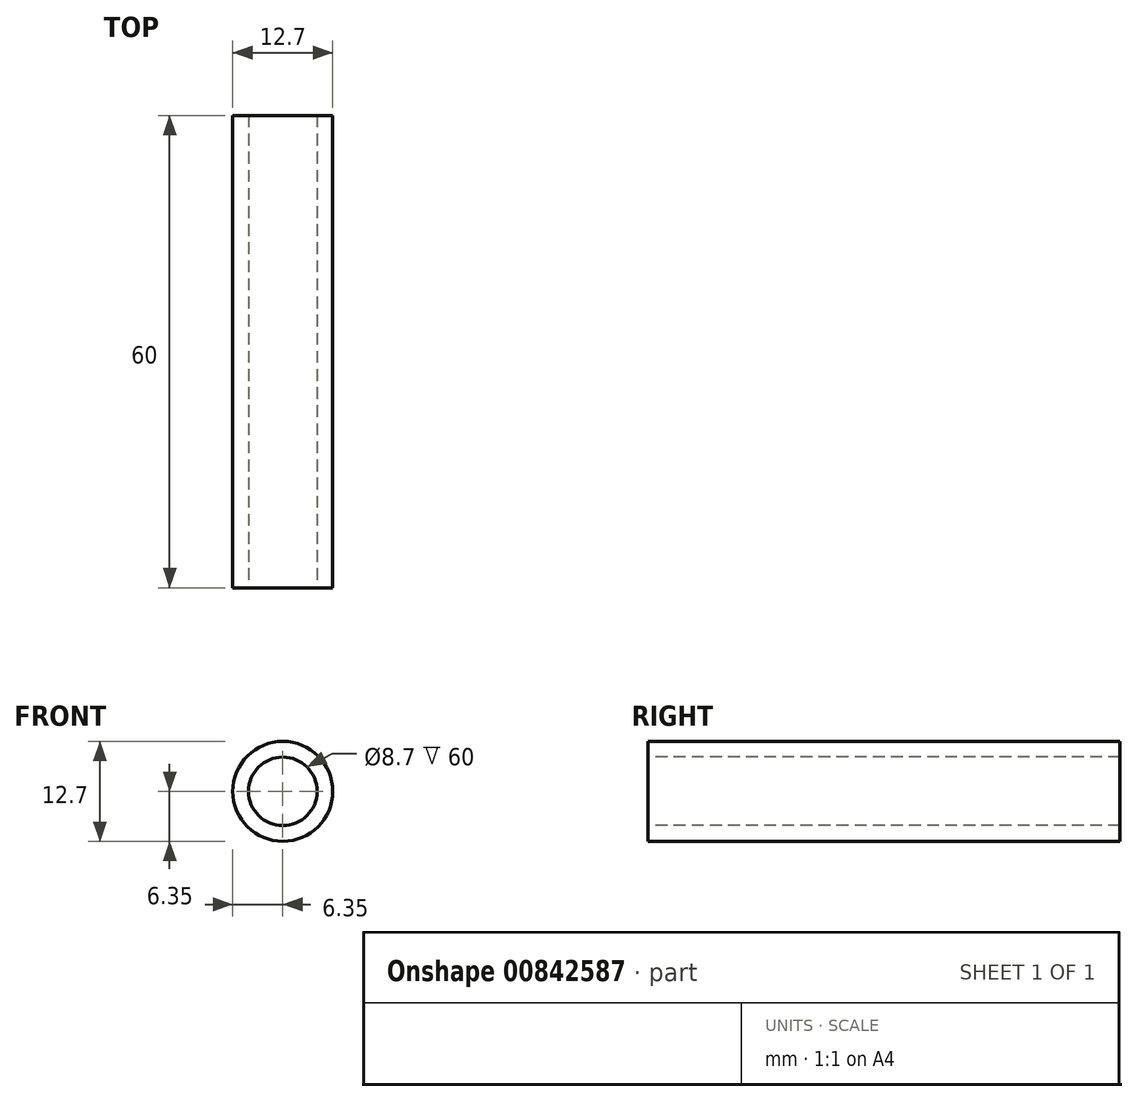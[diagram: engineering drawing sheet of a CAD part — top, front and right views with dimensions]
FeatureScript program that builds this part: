
annotation { "Feature Type Name" : "Feature", "Feature Type Description" : "" }
export const myFeature = defineFeature(function(context is Context, id is Id, definition is map)
    precondition{}
    {
        {
            var Q0;
            Q0=qCreatedBy(makeId("Front.planeOp"),FACE);
            var sketch = newSketch(context, id + "F0", { "sketchPlane" : qUnion([Q0])});
            skCircle(sketch, "E0", {"center": v(0, 0) * mm, "radius": 6.35 * mm});
            skCircle(sketch, "E1", {"center": v(0, 0) * mm, "radius": 4.35 * mm});
            skSolve(sketch);
        }
        {
            var Q0;
            Q0 = qSketchRegion(id + "F0", true);
            extrude(context, id + "F1", {"entities" : qUnion([Q0]), "oppositeDirection" : true, "depth" : 60 * mm, "offsetDistance" : 25.4 * mm});
        }
    });
